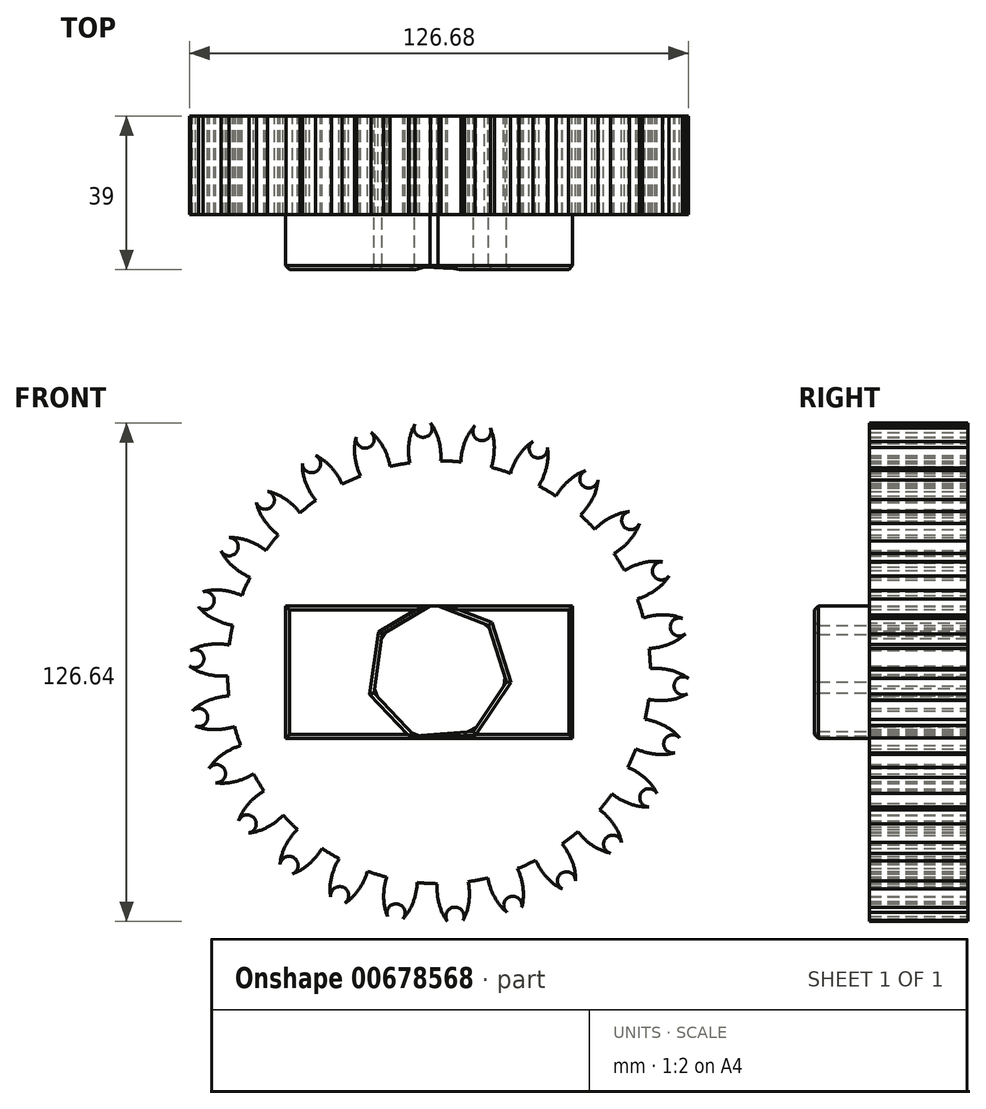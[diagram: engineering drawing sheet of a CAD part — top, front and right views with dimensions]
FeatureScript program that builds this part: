
annotation { "Feature Type Name" : "Feature", "Feature Type Description" : "" }
export const myFeature = defineFeature(function(context is Context, id is Id, definition is map)
    precondition{}
    {
        {
            var Q0;
            Q0=qCreatedBy(makeId("Front.planeOp"),FACE);
            var sketch = newSketch(context, id + "F0", { "sketchPlane" : qUnion([Q0])});
            skCircle(sketch, "E0", {"center": v(0, 0) * mm, "radius": 53.72 * mm});
            skCircle(sketch, "E1", {"center": v(0, 0) * mm, "radius": 58.67 * mm, "construction": true});
            skCircle(sketch, "E2", {"center": v(0, 0) * mm, "radius": 63.5 * mm, "construction": true});
            skLineSegment(sketch, "E3", {"start": v(0, 0) * mm, "end": v(0, 82.02) * mm, "construction": true});
            skLineSegment(sketch, "E4", {"start": v(0, 0) * mm, "end": v(-6.25, 95.9) * mm, "construction": true});
            skLineSegment(sketch, "E5", {"start": v(0, 58.67) * mm, "end": v(-47.3, 58.67) * mm, "construction": true});
            skLineSegment(sketch, "E6", {"start": v(-3.83, 58.67) * mm, "end": v(-76.9, 32.08) * mm, "construction": true});
            skCircle(sketch, "E7", {"center": v(0, 0) * mm, "radius": 56.44 * mm, "construction": true});
            skCircle(sketch, "E8", {"center": v(0, 58.67) * mm, "radius": 14.6 * mm, "construction": true});
            skCircle(sketch, "E9", {"center": v(-14.12, 54.93) * mm, "radius": 14.6 * mm, "construction": true});
            skArc(sketch, "E10", {"start": v(0, 58.67) * mm, "mid": v(-0.87, 61.2) * mm, "end": v(-2.26, 63.46) * mm});
            skArc(sketch, "E11", {"start": v(0.44, 53.72) * mm, "mid": v(0.42, 56.21) * mm, "end": v(0, 58.67) * mm});
            skArc(sketch, "E12.MirrorCS", {"start": v(-7.62, 58.18) * mm, "mid": v(-7.09, 60.78) * mm, "end": v(-6, 63.22) * mm});
            skArc(sketch, "E13.MirrorCS", {"start": v(-7.41, 53.2) * mm, "mid": v(-7.72, 55.68) * mm, "end": v(-7.62, 58.18) * mm});
            skArc(sketch, "E14", {"start": v(-6, 63.22) * mm, "mid": v(-3.9, 59.69) * mm, "end": v(-2.26, 63.46) * mm});
            skLineSegment(sketch, "E15.bottom", {"start": v(0, 11.33) * mm, "end": v(-2.48, 11.33) * mm});
            skLineSegment(sketch, "E15.top", {"start": v(0, 0) * mm, "end": v(-2.48, 0) * mm});
            skLineSegment(sketch, "E15.left", {"start": v(0, 11.33) * mm, "end": v(0, 0) * mm});
            skLineSegment(sketch, "E16.bottom", {"start": v(33.97, 16.84) * mm, "end": v(-38.94, 16.84) * mm});
            skLineSegment(sketch, "E16.top", {"start": v(33.97, -16.84) * mm, "end": v(-38.94, -16.84) * mm});
            skLineSegment(sketch, "E16.left", {"start": v(33.97, 16.84) * mm, "end": v(33.97, -16.84) * mm});
            skLineSegment(sketch, "E16.right", {"start": v(-38.94, 16.84) * mm, "end": v(-38.94, -16.84) * mm});
            skPoint(sketch, "E16.middle", {"position": v(-2.48, 0) * mm});
            skCircle(sketch, "E17.cCircle", {"center": v(0, 0) * mm, "radius": 15.66 * mm, "construction": true});
            skLineSegment(sketch, "E17.0", {"start": v(17.2, -2.44) * mm, "end": v(8.82, -14.97) * mm});
            skLineSegment(sketch, "E17.1", {"start": v(8.82, -14.97) * mm, "end": v(-6.2, -16.23) * mm});
            skLineSegment(sketch, "E17.2", {"start": v(-6.2, -16.23) * mm, "end": v(-16.56, -5.27) * mm});
            skLineSegment(sketch, "E17.3", {"start": v(-16.56, -5.27) * mm, "end": v(-14.45, 9.66) * mm});
            skLineSegment(sketch, "E17.4", {"start": v(-14.45, 9.66) * mm, "end": v(-1.45, 17.32) * mm});
            skLineSegment(sketch, "E17.5", {"start": v(-1.45, 17.32) * mm, "end": v(12.63, 11.93) * mm});
            skLineSegment(sketch, "E17.6", {"start": v(12.63, 11.93) * mm, "end": v(17.2, -2.44) * mm});
            skPoint(sketch, "E17.0.midPoint", {"position": v(13.02, -8.7) * mm});
            skSolve(sketch);
        }
        {
            var Q0;
            Q0=makeQuery(id+"F0.imprint","IMPRINT",FACE,{"disambiguationData":[TD([[makeQuery(id+"F0.imprint","IMPRINT",EDGE,{"derivedFrom":sQuery(id+"F0.wireOp",EDGE,"E16.top")}),1.0]])]});
            var Q1;
            {var subQ0=sQuery(id+"F0.wireOp",EDGE,"E11");Q1=makeQuery(id+"F0.imprint","IMPRINT",FACE,{"disambiguationData":[TD([[makeQuery(id+"F0.imprint","IMPRINT",EDGE,{"derivedFrom":subQ0}),1.0]])]});}
            extrude(context, id + "F1", {"entities" : qUnion([Q0, Q1]), "depth" : 25 * mm, "offsetDistance" : 25 * mm});
        }
        {
            var Q0;
            Q0=makeQuery(id+"F1.opExtrude","SWEPT_BODY",BODY,{"disambiguationData":[OSD([sQuery(id+"F0.wireOp",EDGE,"E0"),sQuery(id+"F0.wireOp",EDGE,"E10"),sQuery(id+"F0.wireOp",EDGE,"E11"),sQuery(id+"F0.wireOp",EDGE,"E12.MirrorCS"),sQuery(id+"F0.wireOp",EDGE,"E13.MirrorCS"),sQuery(id+"F0.wireOp",EDGE,"E14"),sQuery(id+"F0.wireOp",EDGE,"E16.bottom"),sQuery(id+"F0.wireOp",EDGE,"E16.top"),sQuery(id+"F0.wireOp",EDGE,"E16.left"),sQuery(id+"F0.wireOp",EDGE,"E16.right"),sQuery(id+"F0.wireOp",EDGE,"E17.4"),sQuery(id+"F0.wireOp",EDGE,"E17.5")])]});
            var Q1;
            Q1=makeQuery(id+"F1.opExtrude","SWEPT_FACE",FACE,{"disambiguationData":[OSD([sQuery(id+"F0.wireOp",EDGE,"E0")])]});
            circularPattern(context, id + "F2", {"entities" : qUnion([Q0]), "axis" : qUnion([Q1]), "angle" : 360 * degree, "instanceCount" : 26, "equalSpace" : true});
        }
        {
            var Q0;
            Q0=makeQuery(id+"F0.imprint","IMPRINT",FACE,{"disambiguationData":[TD([[makeQuery(id+"F0.imprint","IMPRINT",EDGE,{"derivedFrom":sQuery(id+"F0.wireOp",EDGE,"E16.top")}),-1.0]])]});
            extrude(context, id + "F3", {"entities" : qUnion([Q0]), "operationType" : NewBodyOperationType.ADD, "depth" : 39 * mm, "offsetDistance" : 25 * mm});
        }
        {
            var Q0;
            Q0=makeQuery(id+"F3.opExtrude","CAP_FACE",FACE,{"disambiguationData":[OSD([sQuery(id+"F0.wireOp",EDGE,"E16.bottom"),sQuery(id+"F0.wireOp",EDGE,"E16.top"),sQuery(id+"F0.wireOp",EDGE,"E16.left"),sQuery(id+"F0.wireOp",EDGE,"E16.right"),sQuery(id+"F0.wireOp",EDGE,"E17.0"),sQuery(id+"F0.wireOp",EDGE,"E17.1"),sQuery(id+"F0.wireOp",EDGE,"E17.2"),sQuery(id+"F0.wireOp",EDGE,"E17.3"),sQuery(id+"F0.wireOp",EDGE,"E17.4"),sQuery(id+"F0.wireOp",EDGE,"E17.5"),sQuery(id+"F0.wireOp",EDGE,"E17.6")])],"isStart":false});
            chamfer(context, id + "F4", {"entities" : qUnion([Q0]), "width" : 1 * mm, "tangentPropagation" : true});
        }
    });
